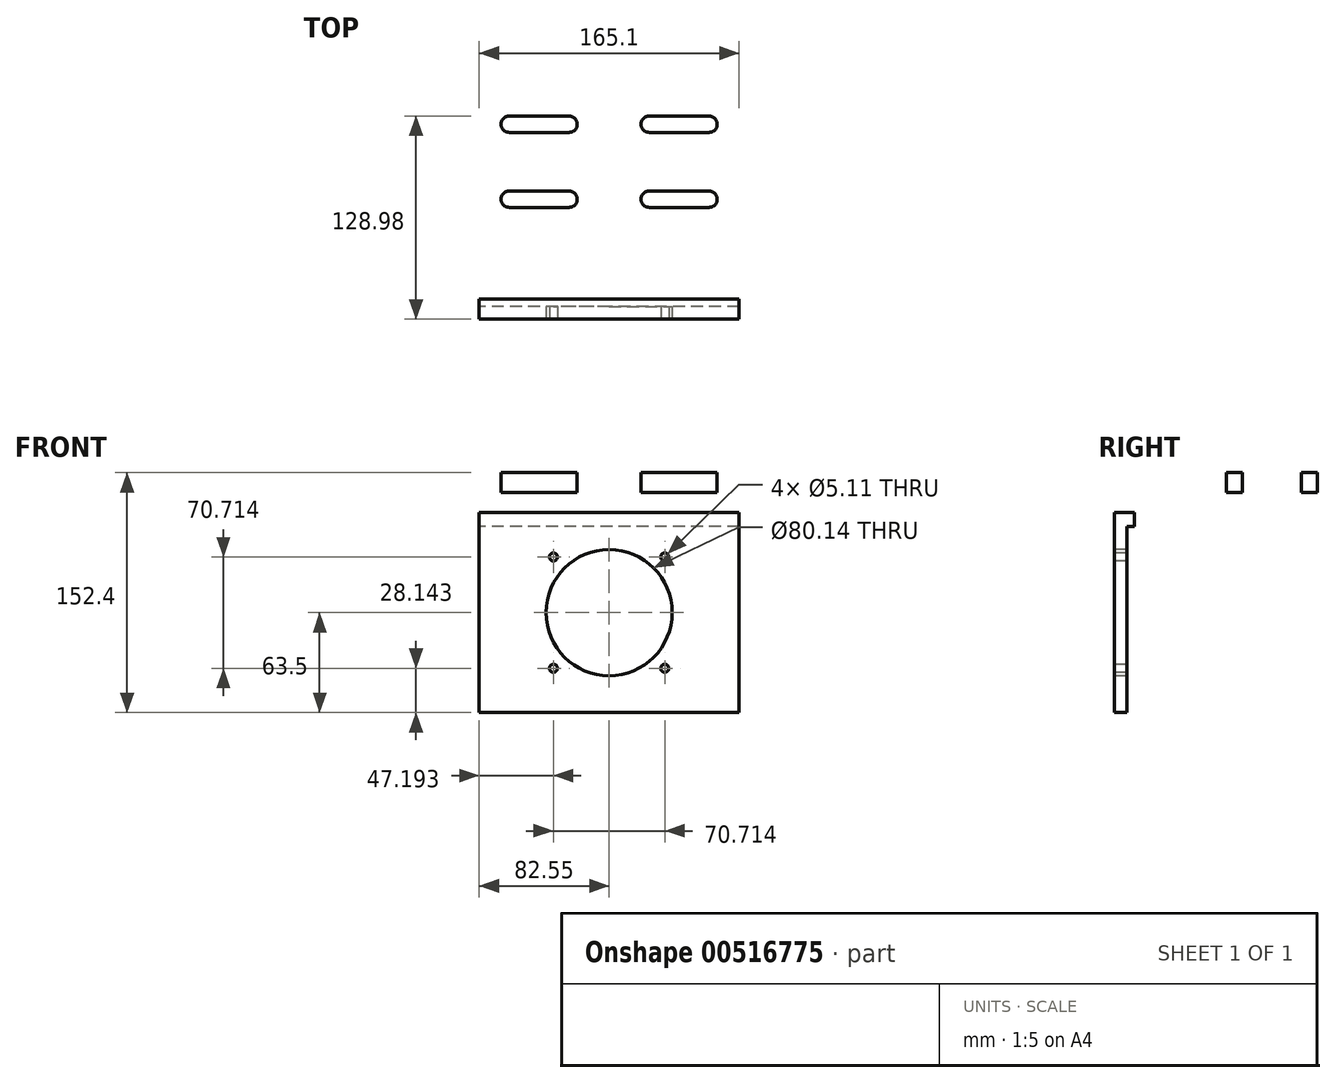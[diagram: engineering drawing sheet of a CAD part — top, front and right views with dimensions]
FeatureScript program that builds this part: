
annotation { "Feature Type Name" : "Feature", "Feature Type Description" : "" }
export const myFeature = defineFeature(function(context is Context, id is Id, definition is map)
    precondition{}
    {
        {
            var Q0;
            Q0=qCreatedBy(makeId("Right.planeOp"),FACE);
            var sketch = newSketch(context, id + "F0", { "sketchPlane" : qUnion([Q0])});
            skLineSegment(sketch, "E0", {"start": v(0, 0) * mm, "end": v(0, 152.4) * mm});
            skLineSegment(sketch, "E1", {"start": v(0, 152.4) * mm, "end": v(152.4, 152.4) * mm});
            skLineSegment(sketch, "E2", {"start": v(152.4, 152.4) * mm, "end": v(152.4, 146.05) * mm});
            skLineSegment(sketch, "E3", {"start": v(146.05, 139.7) * mm, "end": v(25.4, 139.7) * mm});
            skLineSegment(sketch, "E4", {"start": v(12.7, 127) * mm, "end": v(12.7, 0) * mm});
            skLineSegment(sketch, "E5", {"start": v(12.7, 0) * mm, "end": v(0, 0) * mm});
            skPoint(sketch, "E6.visualSharp", {"position": v(12.7, 139.7) * mm});
            skArc(sketch, "E6.filletArc", {"start": v(25.4, 139.7) * mm, "mid": v(16.42, 135.98) * mm, "end": v(12.7, 127) * mm});
            skPoint(sketch, "E7.visualSharp", {"position": v(152.4, 139.7) * mm});
            skArc(sketch, "E7.filletArc", {"start": v(146.05, 139.7) * mm, "mid": v(150.54, 141.56) * mm, "end": v(152.4, 146.05) * mm});
            skSolve(sketch);
        }
        {
            var Q0;
            Q0=makeQuery(id+"F0.imprint","IMPRINT",FACE,{"disambiguationData":[TD([[makeQuery(id+"F0.imprint","IMPRINT",EDGE,{"derivedFrom":sQuery(id+"F0.wireOp",EDGE,"E0")}),-1.0]])]});
            extrude(context, id + "F1", {"entities" : qUnion([Q0]), "depth" : 165.1 * mm, "offsetDistance" : 25.4 * mm});
        }
        {
            var Q0;
            Q0=makeQuery(id+"F1.opExtrude","SWEPT_FACE",FACE,{"disambiguationData":[OSD([sQuery(id+"F0.wireOp",EDGE,"E0")])]});
            var sketch = newSketch(context, id + "F2", { "sketchPlane" : qUnion([Q0])});
            skPoint(sketch, "E8", {"position": v(82.55, 63.5) * mm});
            skCircle(sketch, "E9", {"center": v(82.55, 63.5) * mm, "radius": 40.07 * mm});
            skSolve(sketch);
        }
        {
            var Q0;
            Q0=makeQuery(id+"F2.imprint","IMPRINT",FACE,{"disambiguationData":[TD([[makeQuery(id+"F2.imprint","IMPRINT",EDGE,{"derivedFrom":sQuery(id+"F2.wireOp",EDGE,"E9")}),1.0]])]});
            extrude(context, id + "F3", {"entities" : qUnion([Q0]), "operationType" : NewBodyOperationType.REMOVE, "oppositeDirection" : true, "depth" : 25.4 * mm, "offsetDistance" : 25.4 * mm});
        }
        {
            var Q0;
            Q0=makeQuery(id+"F1.opExtrude","SWEPT_FACE",FACE,{"disambiguationData":[OSD([sQuery(id+"F0.wireOp",EDGE,"E0")])]});
            var sketch = newSketch(context, id + "F4", { "sketchPlane" : qUnion([Q0])});
            skPoint(sketch, "E10", {"position": v(82.55, 63.5) * mm});
            skPoint(sketch, "E11", {"position": v(41.28, 104.77) * mm});
            skPoint(sketch, "E12", {"position": v(123.83, 104.78) * mm});
            skPoint(sketch, "E13", {"position": v(123.83, 22.22) * mm});
            skPoint(sketch, "E14", {"position": v(41.28, 22.22) * mm});
            skSolve(sketch);
        }
        {
            var Q0;
            {var subQ0=sQuery(id+"F0.wireOp",EDGE,"E0");Q0=makeQuery(id+"F4.imprint","IMPRINT",FACE,{"disambiguationData":[TD([[makeQuery(id+"F4.imprint","IMPRINT",EDGE,{"derivedFrom":makeQuery(id+"F1.opExtrude","CAP_EDGE",EDGE,{"disambiguationData":[OSD([subQ0])],"isStart":true})}),-1.0]])]});}
            var sketch = newSketch(context, id + "F5", { "sketchPlane" : qUnion([Q0])});
            skPoint(sketch, "E15", {"position": v(47.2, 98.86) * mm});
            skPoint(sketch, "E16", {"position": v(117.9, 98.86) * mm});
            skPoint(sketch, "E17", {"position": v(117.9, 28.14) * mm});
            skPoint(sketch, "E18", {"position": v(47.2, 28.14) * mm});
            skSolve(sketch);
        }
        {
            var Q0;
            Q0=sQuery(id+"F5.wireOp",VERTEX,"E15");
            var Q1;
            Q1=sQuery(id+"F5.wireOp",VERTEX,"E16");
            var Q2;
            Q2=sQuery(id+"F5.wireOp",VERTEX,"E17");
            var Q3;
            Q3=sQuery(id+"F5.wireOp",VERTEX,"E18");
            var Q4;
            Q4=makeQuery(id+"F1.opExtrude","SWEPT_BODY",BODY,{"disambiguationData":[OSD([sQuery(id+"F0.wireOp",EDGE,"E0"),sQuery(id+"F0.wireOp",EDGE,"E1"),sQuery(id+"F0.wireOp",EDGE,"E2"),sQuery(id+"F0.wireOp",EDGE,"E3"),sQuery(id+"F0.wireOp",EDGE,"E4"),sQuery(id+"F0.wireOp",EDGE,"E5"),sQuery(id+"F0.wireOp",EDGE,"b833c1c2-638b-4f6e-8f8b-8b8cb02ea66f.filletArc"),sQuery(id+"F0.wireOp",EDGE,"E6.filletArc")])]});
            hole(context, id + "F6", {"style" : HoleStyle.SIMPLE, "endStyle" : HoleEndStyle.THROUGH, "standardTappedOrClearance" : lookupTablePath({ "standard" : "ANSI", "engagement" : "75%", "pitch" : "20 tpi", "size" : "1/4", "type" : "Tapped" }), "standardBlindInLast" : lookupTablePath({ "standard" : "ANSI", "engagement" : "75%", "pitch" : "20 tpi", "size" : "1/4", "type" : "Tapped" }), "holeDiameter" : 5.1 * mm, "showTappedDepth" : true, "isTappedThrough" : true, "tappedDepth" : 8.9 * mm, "tapClearance" : 1, "locations" : qUnion([Q0, Q1, Q2, Q3]), "scope" : qUnion([Q4]), "majorDiameter" : 6.35 * mm});
        }
        {
            var Q0;
            Q0=makeQuery(id+"F4.imprint","IMPRINT",FACE,{"disambiguationData":[TD([[makeQuery(id+"F4.imprint","IMPRINT",EDGE,{"derivedFrom":makeQuery(id+"F3.boolean.opBoolean","COPY",EDGE,{"derivedFrom":makeQuery(id+"F3.opExtrude","CAP_EDGE",EDGE,{"disambiguationData":[OSD([sQuery(id+"F2.wireOp",EDGE,"E9")])],"isStart":true})})}),1.0]])]});
            var sketch = newSketch(context, id + "F7", { "sketchPlane" : qUnion([Q0])});
            skCircle(sketch, "E19", {"center": v(82.55, 63.5) * mm, "radius": 40.07 * mm});
            skSolve(sketch);
        }
        {
            var Q0;
            Q0=makeQuery(id+"F1.opExtrude","SWEPT_FACE",FACE,{"disambiguationData":[OSD([sQuery(id+"F0.wireOp",EDGE,"E1")])]});
            var sketch = newSketch(context, id + "F8", { "sketchPlane" : qUnion([Q0])});
            skLineSegment(sketch, "E20", {"start": v(19.05, 76.2) * mm, "end": v(57.15, 76.2) * mm});
            skLineSegment(sketch, "E21", {"start": v(107.95, 76.2) * mm, "end": v(146.05, 76.2) * mm});
            skLineSegment(sketch, "E22", {"start": v(19.05, 123.83) * mm, "end": v(57.15, 123.83) * mm});
            skLineSegment(sketch, "E23", {"start": v(107.95, 123.83) * mm, "end": v(146.05, 123.83) * mm});
            skArc(sketch, "E24.0.startCap", {"start": v(19.05, 118.67) * mm, "mid": v(13.9, 123.83) * mm, "end": v(19.05, 128.98) * mm});
            skArc(sketch, "E24.0.endCap", {"start": v(57.15, 128.98) * mm, "mid": v(62.3, 123.83) * mm, "end": v(57.15, 118.67) * mm});
            skLineSegment(sketch, "E24.0.left", {"start": v(19.05, 128.98) * mm, "end": v(57.15, 128.98) * mm});
            skLineSegment(sketch, "E24.0.right", {"start": v(19.05, 118.67) * mm, "end": v(57.15, 118.67) * mm});
            skArc(sketch, "E25.0.startCap", {"start": v(107.95, 118.67) * mm, "mid": v(102.8, 123.83) * mm, "end": v(107.95, 128.98) * mm});
            skArc(sketch, "E25.0.endCap", {"start": v(146.05, 128.98) * mm, "mid": v(151.2, 123.83) * mm, "end": v(146.05, 118.67) * mm});
            skLineSegment(sketch, "E25.0.left", {"start": v(107.95, 128.98) * mm, "end": v(146.05, 128.98) * mm});
            skLineSegment(sketch, "E25.0.right", {"start": v(107.95, 118.67) * mm, "end": v(146.05, 118.67) * mm});
            skArc(sketch, "E26.0.startCap", {"start": v(107.95, 71.04) * mm, "mid": v(102.8, 76.2) * mm, "end": v(107.95, 81.36) * mm});
            skArc(sketch, "E26.0.endCap", {"start": v(146.05, 81.36) * mm, "mid": v(151.2, 76.2) * mm, "end": v(146.05, 71.04) * mm});
            skLineSegment(sketch, "E26.0.left", {"start": v(107.95, 81.36) * mm, "end": v(146.05, 81.36) * mm});
            skLineSegment(sketch, "E26.0.right", {"start": v(107.95, 71.04) * mm, "end": v(146.05, 71.04) * mm});
            skArc(sketch, "E27.0.startCap", {"start": v(19.05, 71.04) * mm, "mid": v(13.9, 76.2) * mm, "end": v(19.05, 81.36) * mm});
            skArc(sketch, "E27.0.endCap", {"start": v(57.15, 81.36) * mm, "mid": v(62.3, 76.2) * mm, "end": v(57.15, 71.04) * mm});
            skLineSegment(sketch, "E27.0.left", {"start": v(19.05, 81.36) * mm, "end": v(57.15, 81.36) * mm});
            skLineSegment(sketch, "E27.0.right", {"start": v(19.05, 71.04) * mm, "end": v(57.15, 71.04) * mm});
            skSolve(sketch);
        }
        {
            var Q0;
            Q0=makeQuery(id+"F8.imprint","IMPRINT",FACE,{"disambiguationData":[TD([[makeQuery(id+"F8.imprint","IMPRINT",EDGE,{"derivedFrom":sQuery(id+"F8.wireOp",EDGE,"E24.0.startCap")}),-1.0]])]});
            var Q1;
            Q1=makeQuery(id+"F8.imprint","IMPRINT",FACE,{"disambiguationData":[TD([[makeQuery(id+"F8.imprint","IMPRINT",EDGE,{"derivedFrom":sQuery(id+"F8.wireOp",EDGE,"E25.0.startCap")}),-1.0]])]});
            var Q2;
            Q2=makeQuery(id+"F8.imprint","IMPRINT",FACE,{"disambiguationData":[TD([[makeQuery(id+"F8.imprint","IMPRINT",EDGE,{"derivedFrom":sQuery(id+"F8.wireOp",EDGE,"E26.0.startCap")}),-1.0]])]});
            var Q3;
            Q3=makeQuery(id+"F8.imprint","IMPRINT",FACE,{"disambiguationData":[TD([[makeQuery(id+"F8.imprint","IMPRINT",EDGE,{"derivedFrom":sQuery(id+"F8.wireOp",EDGE,"E27.0.startCap")}),-1.0]])]});
            extrude(context, id + "F9", {"entities" : qUnion([Q0, Q1, Q2, Q3]), "operationType" : NewBodyOperationType.REMOVE, "oppositeDirection" : true, "depth" : 25.4 * mm, "offsetDistance" : 25.4 * mm});
        }
        {
            var Q0;
            Q0=makeQuery(id+"F1.opExtrude","SWEPT_FACE",FACE,{"disambiguationData":[OSD([sQuery(id+"F0.wireOp",EDGE,"E4")])]});
            var sketch = newSketch(context, id + "F10", { "sketchPlane" : qUnion([Q0])});
            skLineSegment(sketch, "E28.bottom", {"start": v(-165.1, 118.26) * mm, "end": v(0, 118.26) * mm});
            skLineSegment(sketch, "E28.top", {"start": v(-165.1, 0) * mm, "end": v(0, 0) * mm});
            skLineSegment(sketch, "E28.left", {"start": v(-165.1, 118.26) * mm, "end": v(-165.1, 0) * mm});
            skLineSegment(sketch, "E28.right", {"start": v(0, 118.26) * mm, "end": v(0, 0) * mm});
            skSolve(sketch);
        }
        {
            var Q0;
            Q0=makeQuery(id+"F10.imprint","IMPRINT",FACE,{"disambiguationData":[TD([[makeQuery(id+"F10.imprint","IMPRINT",EDGE,{"derivedFrom":sQuery(id+"F10.wireOp",EDGE,"E28.bottom")}),-1.0]])]});
            extrude(context, id + "F11", {"entities" : qUnion([Q0]), "operationType" : NewBodyOperationType.REMOVE, "oppositeDirection" : true, "depth" : 4.75 * mm, "offsetDistance" : 25.4 * mm});
        }
    });
